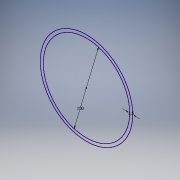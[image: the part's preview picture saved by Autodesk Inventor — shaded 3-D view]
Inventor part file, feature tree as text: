
AUTODESK INVENTOR PART (.ipt)
format: ipt  version: 2016 (Build 200138000, 138)  size: 96,768 bytes
history: native  units: mm
features: extrude x1, sketch x1
ambient origin geometry x8: Origin, YZ Plane, XZ Plane, XY Plane, X Axis, Y Axis, Z Axis, Center Point
bodies: Solid1 (feature_tree)
feature tree (2):
  extrude  "Extrusion1"  Depth=400.0mm
  sketch  "Sketch1"  dims[d0=100.0mm d1=3.5mm d2=400.0mm d3=0.0mm]
